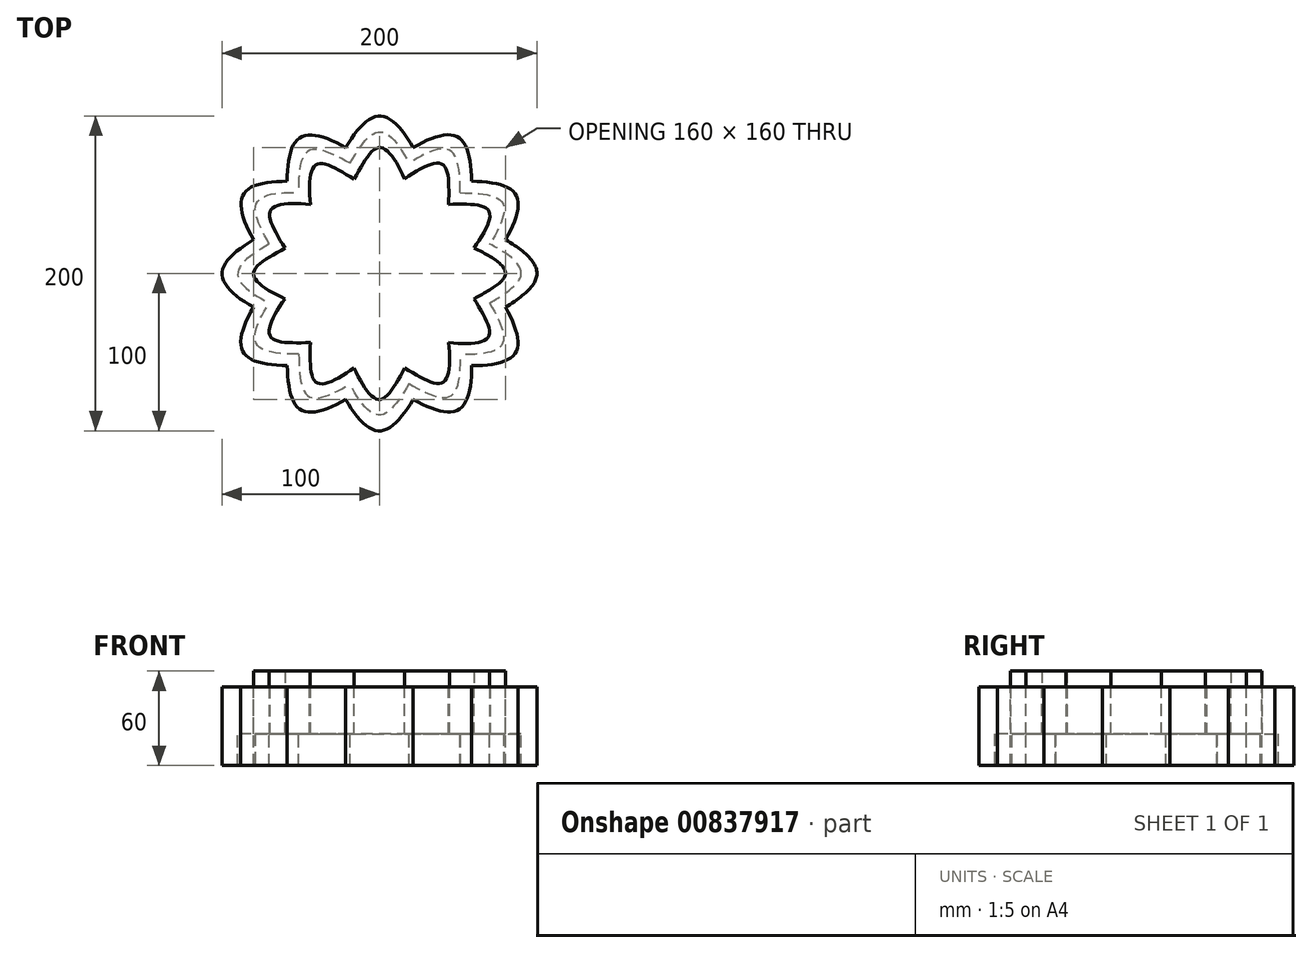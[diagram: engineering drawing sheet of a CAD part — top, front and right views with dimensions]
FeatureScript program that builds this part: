
annotation { "Feature Type Name" : "Feature", "Feature Type Description" : "" }
export const myFeature = defineFeature(function(context is Context, id is Id, definition is map)
    precondition{}
    {
        {
            var Q0;
            Q0=qCreatedBy(makeId("Top.planeOp"),FACE);
            var sketch = newSketch(context, id + "F0", { "sketchPlane" : qUnion([Q0])});
            skLineSegment(sketch, "E0.18.0", {"start": v(0, 0) * mm, "end": v(130, 0) * mm});
            skPoint(sketch, "E0.center", {"position": v(0, 0) * mm});
            skFitSpline(sketch, "E1", {"points": [v(-29.47, 110) * mm, v(0, 130) * mm, v(29.47, 110) * mm], "startDerivative": vector(57.37, 68.98) * mm, "endDerivative": vector(57.3, -69.1) * mm});
            skFitSpline(sketch, "E2", {"points": [v(-26.8, 100) * mm, v(0, 120) * mm, v(26.8, 100) * mm], "startDerivative": vector(51.28, 69.17) * mm, "endDerivative": vector(53.62, -65.87) * mm});
            skFitSpline(sketch, "E3", {"points": [v(-24.12, 90) * mm, v(0, 110) * mm, v(24.12, 90) * mm], "startDerivative": vector(46.86, 68.47) * mm, "endDerivative": vector(46.36, -69.15) * mm});
            skFitSpline(sketch, "E4", {"points": [v(-21.44, 80) * mm, v(0, 100) * mm, v(21.44, 80) * mm], "startDerivative": vector(41.41, 68.36) * mm, "endDerivative": vector(39.83, -70.42) * mm});
            skFitSpline(sketch, "E5", {"points": [v(-18.76, 70) * mm, v(0, 90) * mm, v(18.76, 70) * mm], "startDerivative": vector(36.89, 61.88) * mm, "endDerivative": vector(33.7, -65.99) * mm});
            skFitSpline(sketch, "E6", {"points": [v(-16.08, 60) * mm, v(0, 80) * mm, v(16.08, 60) * mm], "startDerivative": vector(32.76, 58.8) * mm, "endDerivative": vector(28.98, -63.6) * mm});
            skFitSpline(sketch, "E7.MirrorCS", {"points": [v(80.53, 80.53) * mm, v(65, 112.58) * mm, v(29.47, 110) * mm], "startDerivative": vector(-15.2, 88.43) * mm, "endDerivative": vector(-84.17, -31.2) * mm});
            skFitSpline(sketch, "E8.MirrorCS", {"points": [v(73.2, 73.2) * mm, v(60, 103.92) * mm, v(26.8, 100) * mm], "startDerivative": vector(-9.83, 85.54) * mm, "endDerivative": vector(-79.37, -30.24) * mm});
            skFitSpline(sketch, "E9.MirrorCS", {"points": [v(65.88, 65.88) * mm, v(55, 95.26) * mm, v(24.12, 90) * mm], "startDerivative": vector(-6.35, 82.73) * mm, "endDerivative": vector(-74.72, -36.7) * mm});
            skFitSpline(sketch, "E10.MirrorCS", {"points": [v(58.56, 58.56) * mm, v(50, 86.6) * mm, v(21.44, 80) * mm], "startDerivative": vector(-1.68, 79.9) * mm, "endDerivative": vector(-69.7, -41.07) * mm});
            skFitSpline(sketch, "E11.MirrorCS", {"points": [v(51.24, 51.24) * mm, v(45, 77.94) * mm, v(18.76, 70) * mm], "startDerivative": vector(-1, 72.03) * mm, "endDerivative": vector(-62.17, -40.3) * mm});
            skFitSpline(sketch, "E12.MirrorCS", {"points": [v(43.92, 43.92) * mm, v(40, 69.28) * mm, v(16.08, 60) * mm], "startDerivative": vector(1.03, 67.31) * mm, "endDerivative": vector(-56.9, -40.6) * mm});
            skFitSpline(sketch, "E13.MirrorCS", {"points": [v(43.92, 43.92) * mm, v(69.28, 40) * mm, v(60, 16.08) * mm], "startDerivative": vector(67.31, 1.03) * mm, "endDerivative": vector(-40.6, -56.9) * mm});
            skFitSpline(sketch, "E14.MirrorCS", {"points": [v(60, -16.08) * mm, v(80, 0) * mm, v(60, 16.08) * mm], "startDerivative": vector(58.8, 32.76) * mm, "endDerivative": vector(-63.6, 28.98) * mm});
            skFitSpline(sketch, "E15.MirrorCS", {"points": [v(70, -18.76) * mm, v(90, 0) * mm, v(70, 18.76) * mm], "startDerivative": vector(61.88, 36.89) * mm, "endDerivative": vector(-65.99, 33.7) * mm});
            skFitSpline(sketch, "E16.MirrorCS", {"points": [v(80, -21.44) * mm, v(100, 0) * mm, v(80, 21.44) * mm], "startDerivative": vector(68.36, 41.41) * mm, "endDerivative": vector(-70.42, 39.83) * mm});
            skFitSpline(sketch, "E17.MirrorCS", {"points": [v(90, -24.12) * mm, v(110, 0) * mm, v(90, 24.12) * mm], "startDerivative": vector(68.47, 46.86) * mm, "endDerivative": vector(-69.15, 46.36) * mm});
            skFitSpline(sketch, "E18.MirrorCS", {"points": [v(100, -26.8) * mm, v(120, 0) * mm, v(100, 26.8) * mm], "startDerivative": vector(69.17, 51.28) * mm, "endDerivative": vector(-65.87, 53.62) * mm});
            skFitSpline(sketch, "E19.MirrorCS", {"points": [v(110, -29.47) * mm, v(130, 0) * mm, v(110, 29.47) * mm], "startDerivative": vector(68.98, 57.37) * mm, "endDerivative": vector(-69.1, 57.3) * mm});
            skFitSpline(sketch, "E20.MirrorCS", {"points": [v(80.53, 80.53) * mm, v(112.58, 65) * mm, v(110, 29.47) * mm], "startDerivative": vector(88.43, -15.2) * mm, "endDerivative": vector(-31.2, -84.17) * mm});
            skFitSpline(sketch, "E21.MirrorCS", {"points": [v(73.2, 73.2) * mm, v(103.92, 60) * mm, v(100, 26.8) * mm], "startDerivative": vector(85.54, -9.83) * mm, "endDerivative": vector(-30.24, -79.37) * mm});
            skFitSpline(sketch, "E22.MirrorCS", {"points": [v(65.88, 65.88) * mm, v(95.26, 55) * mm, v(90, 24.12) * mm], "startDerivative": vector(82.73, -6.35) * mm, "endDerivative": vector(-36.7, -74.72) * mm});
            skFitSpline(sketch, "E23.MirrorCS", {"points": [v(58.56, 58.56) * mm, v(86.6, 50) * mm, v(80, 21.44) * mm], "startDerivative": vector(79.9, -1.68) * mm, "endDerivative": vector(-41.07, -69.7) * mm});
            skFitSpline(sketch, "E24.MirrorCS", {"points": [v(51.24, 51.24) * mm, v(77.94, 45) * mm, v(70, 18.76) * mm], "startDerivative": vector(72.03, -1) * mm, "endDerivative": vector(-40.3, -62.17) * mm});
            skFitSpline(sketch, "E25.MirrorCS", {"points": [v(-29.47, 110) * mm, v(-65, 112.58) * mm, v(-80.53, 80.53) * mm], "startDerivative": vector(-84.18, 31.06) * mm, "endDerivative": vector(-15.07, -88.49) * mm});
            skFitSpline(sketch, "E26.MirrorCS", {"points": [v(-110, 29.47) * mm, v(-112.58, 65) * mm, v(-80.53, 80.53) * mm], "startDerivative": vector(-31.06, 84.18) * mm, "endDerivative": vector(88.49, 15.07) * mm});
            skFitSpline(sketch, "E27.MirrorCS", {"points": [v(-110, 29.47) * mm, v(-130, 0) * mm, v(-110, -29.47) * mm], "startDerivative": vector(-68.98, -57.37) * mm, "endDerivative": vector(69.1, -57.3) * mm});
            skFitSpline(sketch, "E28.MirrorCS", {"points": [v(-80.53, -80.53) * mm, v(-112.58, -65) * mm, v(-110, -29.47) * mm], "startDerivative": vector(-88.43, 15.2) * mm, "endDerivative": vector(31.2, 84.17) * mm});
            skFitSpline(sketch, "E29.MirrorCS", {"points": [v(-26.8, 100) * mm, v(-60, 103.92) * mm, v(-73.2, 73.2) * mm], "startDerivative": vector(-79, 34.26) * mm, "endDerivative": vector(-13.5, -83.86) * mm});
            skFitSpline(sketch, "E30.MirrorCS", {"points": [v(-24.12, 90) * mm, v(-55, 95.26) * mm, v(-65.88, 65.88) * mm], "startDerivative": vector(-74.82, 35.87) * mm, "endDerivative": vector(-5.58, -83.07) * mm});
            skFitSpline(sketch, "E31.MirrorCS", {"points": [v(-21.44, 80) * mm, v(-50, 86.6) * mm, v(-58.56, 58.56) * mm], "startDerivative": vector(-70.04, 38.5) * mm, "endDerivative": vector(0.71, -80.9) * mm});
            skFitSpline(sketch, "E32.MirrorCS", {"points": [v(-18.76, 70) * mm, v(-45, 77.94) * mm, v(-51.24, 51.24) * mm], "startDerivative": vector(-62.89, 35.14) * mm, "endDerivative": vector(3.82, -74) * mm});
            skFitSpline(sketch, "E33.MirrorCS", {"points": [v(-16.08, 60) * mm, v(-40, 69.28) * mm, v(-43.92, 43.92) * mm], "startDerivative": vector(-57.78, 34.55) * mm, "endDerivative": vector(6.7, -69.57) * mm});
            skFitSpline(sketch, "E34.MirrorCS", {"points": [v(-60, 16.08) * mm, v(-69.28, 40) * mm, v(-43.92, 43.92) * mm], "startDerivative": vector(-34.55, 57.78) * mm, "endDerivative": vector(69.57, -6.7) * mm});
            skFitSpline(sketch, "E35.MirrorCS", {"points": [v(-70, 18.76) * mm, v(-77.94, 45) * mm, v(-51.24, 51.24) * mm], "startDerivative": vector(-35.14, 62.89) * mm, "endDerivative": vector(74, -3.82) * mm});
            skFitSpline(sketch, "E36.MirrorCS", {"points": [v(-80, 21.44) * mm, v(-86.6, 50) * mm, v(-58.56, 58.56) * mm], "startDerivative": vector(-38.5, 70.04) * mm, "endDerivative": vector(80.9, -0.71) * mm});
            skFitSpline(sketch, "E37.MirrorCS", {"points": [v(-90, 24.12) * mm, v(-95.26, 55) * mm, v(-65.88, 65.88) * mm], "startDerivative": vector(-35.87, 74.82) * mm, "endDerivative": vector(83.07, 5.58) * mm});
            skFitSpline(sketch, "E38.MirrorCS", {"points": [v(-100, 26.8) * mm, v(-103.92, 60) * mm, v(-73.2, 73.2) * mm], "startDerivative": vector(-34.26, 79) * mm, "endDerivative": vector(83.86, 13.5) * mm});
            skFitSpline(sketch, "E39.MirrorCS", {"points": [v(-100, 26.8) * mm, v(-120, 0) * mm, v(-100, -26.8) * mm], "startDerivative": vector(-69.17, -51.28) * mm, "endDerivative": vector(65.87, -53.62) * mm});
            skFitSpline(sketch, "E40.MirrorCS", {"points": [v(-90, 24.12) * mm, v(-110, 0) * mm, v(-90, -24.12) * mm], "startDerivative": vector(-68.47, -46.86) * mm, "endDerivative": vector(69.15, -46.36) * mm});
            skFitSpline(sketch, "E41.MirrorCS", {"points": [v(-80, 21.44) * mm, v(-100, 0) * mm, v(-80, -21.44) * mm], "startDerivative": vector(-68.36, -41.41) * mm, "endDerivative": vector(70.42, -39.83) * mm});
            skFitSpline(sketch, "E42.MirrorCS", {"points": [v(-70, 18.76) * mm, v(-90, 0) * mm, v(-70, -18.76) * mm], "startDerivative": vector(-61.88, -36.89) * mm, "endDerivative": vector(65.99, -33.7) * mm});
            skFitSpline(sketch, "E43.MirrorCS", {"points": [v(-60, 16.08) * mm, v(-80, 0) * mm, v(-60, -16.08) * mm], "startDerivative": vector(-58.8, -32.76) * mm, "endDerivative": vector(63.6, -28.98) * mm});
            skFitSpline(sketch, "E44.MirrorCS", {"points": [v(-43.92, -43.92) * mm, v(-69.28, -40) * mm, v(-60, -16.08) * mm], "startDerivative": vector(-67.31, -1.03) * mm, "endDerivative": vector(40.6, 56.9) * mm});
            skFitSpline(sketch, "E45.MirrorCS", {"points": [v(-51.24, -51.24) * mm, v(-77.94, -45) * mm, v(-70, -18.76) * mm], "startDerivative": vector(-72.03, 1) * mm, "endDerivative": vector(40.3, 62.17) * mm});
            skFitSpline(sketch, "E46.MirrorCS", {"points": [v(-58.56, -58.56) * mm, v(-86.6, -50) * mm, v(-80, -21.44) * mm], "startDerivative": vector(-79.9, 1.68) * mm, "endDerivative": vector(41.07, 69.7) * mm});
            skFitSpline(sketch, "E47.MirrorCS", {"points": [v(-65.88, -65.88) * mm, v(-95.26, -55) * mm, v(-90, -24.12) * mm], "startDerivative": vector(-82.73, 6.35) * mm, "endDerivative": vector(36.7, 74.72) * mm});
            skFitSpline(sketch, "E48.MirrorCS", {"points": [v(-73.2, -73.2) * mm, v(-103.92, -60) * mm, v(-100, -26.8) * mm], "startDerivative": vector(-85.54, 9.83) * mm, "endDerivative": vector(30.24, 79.37) * mm});
            skFitSpline(sketch, "E49.MirrorCS", {"points": [v(-43.92, -43.92) * mm, v(-40, -69.28) * mm, v(-16.08, -60) * mm], "startDerivative": vector(-1.03, -67.31) * mm, "endDerivative": vector(56.9, 40.6) * mm});
            skFitSpline(sketch, "E50.MirrorCS", {"points": [v(-51.24, -51.24) * mm, v(-45, -77.94) * mm, v(-18.76, -70) * mm], "startDerivative": vector(1, -72.03) * mm, "endDerivative": vector(62.17, 40.3) * mm});
            skFitSpline(sketch, "E51.MirrorCS", {"points": [v(-58.56, -58.56) * mm, v(-50, -86.6) * mm, v(-21.44, -80) * mm], "startDerivative": vector(1.68, -79.9) * mm, "endDerivative": vector(69.7, 41.07) * mm});
            skFitSpline(sketch, "E52.MirrorCS", {"points": [v(-65.88, -65.88) * mm, v(-55, -95.26) * mm, v(-24.12, -90) * mm], "startDerivative": vector(6.35, -82.73) * mm, "endDerivative": vector(74.72, 36.7) * mm});
            skFitSpline(sketch, "E53.MirrorCS", {"points": [v(-73.2, -73.2) * mm, v(-60, -103.92) * mm, v(-26.8, -100) * mm], "startDerivative": vector(9.83, -85.54) * mm, "endDerivative": vector(79.37, 30.24) * mm});
            skFitSpline(sketch, "E54.MirrorCS", {"points": [v(-80.53, -80.53) * mm, v(-65, -112.58) * mm, v(-29.47, -110) * mm], "startDerivative": vector(15.2, -88.43) * mm, "endDerivative": vector(84.17, 31.2) * mm});
            skFitSpline(sketch, "E55.MirrorCS", {"points": [v(29.47, -110) * mm, v(0, -130) * mm, v(-29.47, -110) * mm], "startDerivative": vector(-57.37, -68.98) * mm, "endDerivative": vector(-57.3, 69.1) * mm});
            skFitSpline(sketch, "E56.MirrorCS", {"points": [v(26.8, -100) * mm, v(0, -120) * mm, v(-26.8, -100) * mm], "startDerivative": vector(-51.28, -69.17) * mm, "endDerivative": vector(-53.62, 65.87) * mm});
            skFitSpline(sketch, "E57.MirrorCS", {"points": [v(24.12, -90) * mm, v(0, -110) * mm, v(-24.12, -90) * mm], "startDerivative": vector(-46.86, -68.47) * mm, "endDerivative": vector(-46.36, 69.15) * mm});
            skFitSpline(sketch, "E58.MirrorCS", {"points": [v(21.44, -80) * mm, v(0, -100) * mm, v(-21.44, -80) * mm], "startDerivative": vector(-41.41, -68.36) * mm, "endDerivative": vector(-39.83, 70.42) * mm});
            skFitSpline(sketch, "E59.MirrorCS", {"points": [v(18.76, -70) * mm, v(0, -90) * mm, v(-18.76, -70) * mm], "startDerivative": vector(-36.89, -61.88) * mm, "endDerivative": vector(-33.7, 65.99) * mm});
            skFitSpline(sketch, "E60.MirrorCS", {"points": [v(16.08, -60) * mm, v(0, -80) * mm, v(-16.08, -60) * mm], "startDerivative": vector(-32.76, -58.8) * mm, "endDerivative": vector(-28.98, 63.6) * mm});
            skFitSpline(sketch, "E61.MirrorCS", {"points": [v(16.08, -60) * mm, v(40, -69.28) * mm, v(43.92, -43.92) * mm], "startDerivative": vector(57.78, -34.55) * mm, "endDerivative": vector(-6.7, 69.57) * mm});
            skFitSpline(sketch, "E62.MirrorCS", {"points": [v(18.76, -70) * mm, v(45, -77.94) * mm, v(51.24, -51.24) * mm], "startDerivative": vector(62.89, -35.14) * mm, "endDerivative": vector(-3.82, 74) * mm});
            skFitSpline(sketch, "E63.MirrorCS", {"points": [v(18.76, -70) * mm, v(45, -77.94) * mm, v(51.24, -51.24) * mm], "startDerivative": vector(62.89, -35.14) * mm, "endDerivative": vector(-3.82, 74) * mm});
            skFitSpline(sketch, "E64.MirrorCS", {"points": [v(60, -16.08) * mm, v(69.28, -40) * mm, v(43.92, -43.92) * mm], "startDerivative": vector(34.55, -57.78) * mm, "endDerivative": vector(-69.57, 6.7) * mm});
            skFitSpline(sketch, "E65.MirrorCS", {"points": [v(70, -18.76) * mm, v(77.94, -45) * mm, v(51.24, -51.24) * mm], "startDerivative": vector(35.14, -62.89) * mm, "endDerivative": vector(-74, 3.82) * mm});
            skFitSpline(sketch, "E66.MirrorCS", {"points": [v(80, -21.44) * mm, v(86.6, -50) * mm, v(58.56, -58.56) * mm], "startDerivative": vector(38.5, -70.04) * mm, "endDerivative": vector(-80.9, 0.71) * mm});
            skFitSpline(sketch, "E67.MirrorCS", {"points": [v(90, -24.12) * mm, v(95.26, -55) * mm, v(65.88, -65.88) * mm], "startDerivative": vector(35.87, -74.82) * mm, "endDerivative": vector(-83.07, -5.58) * mm});
            skFitSpline(sketch, "E68.MirrorCS", {"points": [v(29.47, -110) * mm, v(65, -112.58) * mm, v(80.53, -80.53) * mm], "startDerivative": vector(84.18, -31.06) * mm, "endDerivative": vector(15.07, 88.49) * mm});
            skFitSpline(sketch, "E69.MirrorCS", {"points": [v(26.8, -100) * mm, v(60, -103.92) * mm, v(73.2, -73.2) * mm], "startDerivative": vector(79, -34.26) * mm, "endDerivative": vector(13.5, 83.86) * mm});
            skFitSpline(sketch, "E70.MirrorCS", {"points": [v(24.12, -90) * mm, v(55, -95.26) * mm, v(65.88, -65.88) * mm], "startDerivative": vector(74.82, -35.87) * mm, "endDerivative": vector(5.58, 83.07) * mm});
            skFitSpline(sketch, "E71.MirrorCS", {"points": [v(110, -29.47) * mm, v(112.58, -65) * mm, v(80.53, -80.53) * mm], "startDerivative": vector(31.06, -84.18) * mm, "endDerivative": vector(-88.49, -15.07) * mm});
            skFitSpline(sketch, "E72.MirrorCS", {"points": [v(100, -26.8) * mm, v(103.92, -60) * mm, v(73.2, -73.2) * mm], "startDerivative": vector(34.26, -79) * mm, "endDerivative": vector(-83.86, -13.5) * mm});
            skFitSpline(sketch, "E73.MirrorCS", {"points": [v(21.44, -80) * mm, v(50, -86.6) * mm, v(58.56, -58.56) * mm], "startDerivative": vector(70.04, -38.5) * mm, "endDerivative": vector(-0.71, 80.9) * mm});
            skSolve(sketch);
        }
        {
            var Q0;
            Q0=makeQuery(id+"F0.imprint","IMPRINT",FACE,{"disambiguationData":[TD([[makeQuery(id+"F0.imprint","IMPRINT",EDGE,{"derivedFrom":sQuery(id+"F0.wireOp",EDGE,"E6")}),-1.0]])]});
            extrude(context, id + "F1", {"entities" : qUnion([Q0]), "depth" : 10 * mm, "offsetDistance" : 25 * mm});
        }
        {
            var Q0;
            Q0=makeQuery(id+"F0.imprint","IMPRINT",FACE,{"disambiguationData":[TD([[makeQuery(id+"F0.imprint","IMPRINT",EDGE,{"derivedFrom":sQuery(id+"F0.wireOp",EDGE,"E5")}),-1.0]])]});
            extrude(context, id + "F2", {"entities" : qUnion([Q0]), "operationType" : NewBodyOperationType.ADD, "oppositeDirection" : true, "depth" : 30 * mm, "offsetDistance" : 25 * mm});
        }
        {
            var Q0;
            Q0=makeQuery(id+"F0.imprint","IMPRINT",FACE,{"disambiguationData":[TD([[makeQuery(id+"F0.imprint","IMPRINT",EDGE,{"derivedFrom":sQuery(id+"F0.wireOp",EDGE,"E4")}),-1.0]])]});
            extrude(context, id + "F3", {"entities" : qUnion([Q0]), "operationType" : NewBodyOperationType.ADD, "oppositeDirection" : true, "depth" : 50 * mm, "offsetDistance" : 25 * mm});
        }
    });
